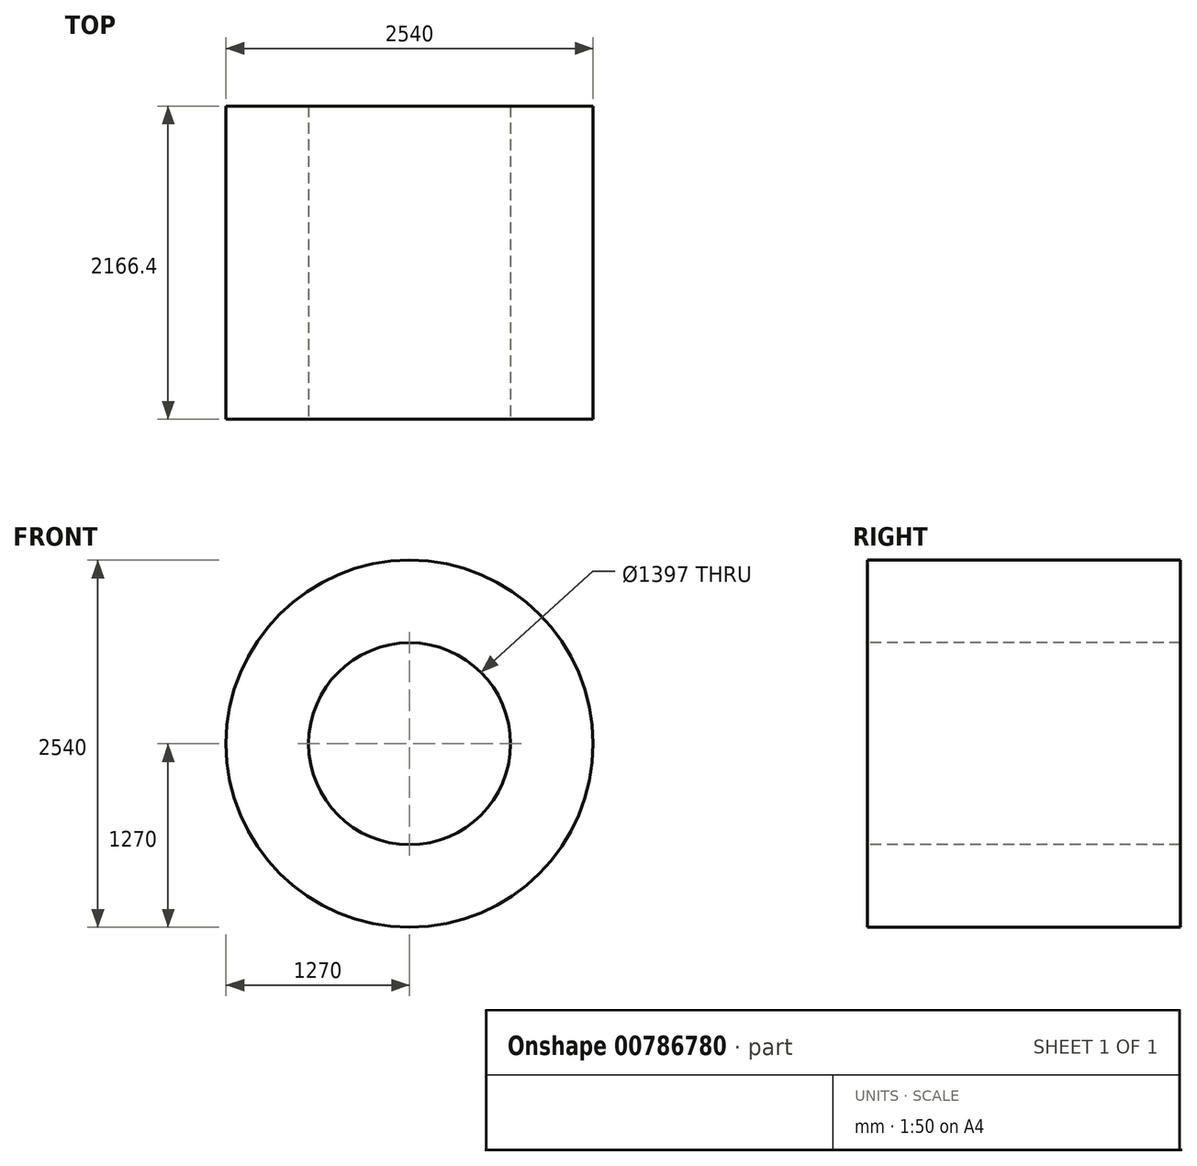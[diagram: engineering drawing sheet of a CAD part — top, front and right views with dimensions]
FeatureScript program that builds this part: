
annotation { "Feature Type Name" : "Feature", "Feature Type Description" : "" }
export const myFeature = defineFeature(function(context is Context, id is Id, definition is map)
    precondition{}
    {
        {
            var Q0;
            Q0=qCreatedBy(makeId("Front.planeOp"),FACE);
            var sketch = newSketch(context, id + "F0", { "sketchPlane" : qUnion([Q0])});
            skCircle(sketch, "E0", {"center": v(698.5, 0) * mm, "radius": 1270 * mm});
            skCircle(sketch, "E1", {"center": v(698.5, 0) * mm, "radius": 698.5 * mm});
            skSolve(sketch);
        }
        {
            var Q0;
            Q0 = qSketchRegion(id + "F0", true);
            var Q1;
            Q1=makeQuery(id+"F0.imprint","IMPRINT",FACE,{"disambiguationData":[TD([[makeQuery(id+"F0.imprint","IMPRINT",EDGE,{"derivedFrom":sQuery(id+"F0.wireOp",EDGE,"E0")}),1.0]])]});
            extrude(context, id + "F1", {"entities" : qUnion([Q0, Q1]), "oppositeDirection" : true, "depth" : 2166.4 * mm, "offsetDistance" : 25.4 * mm});
        }
    });
